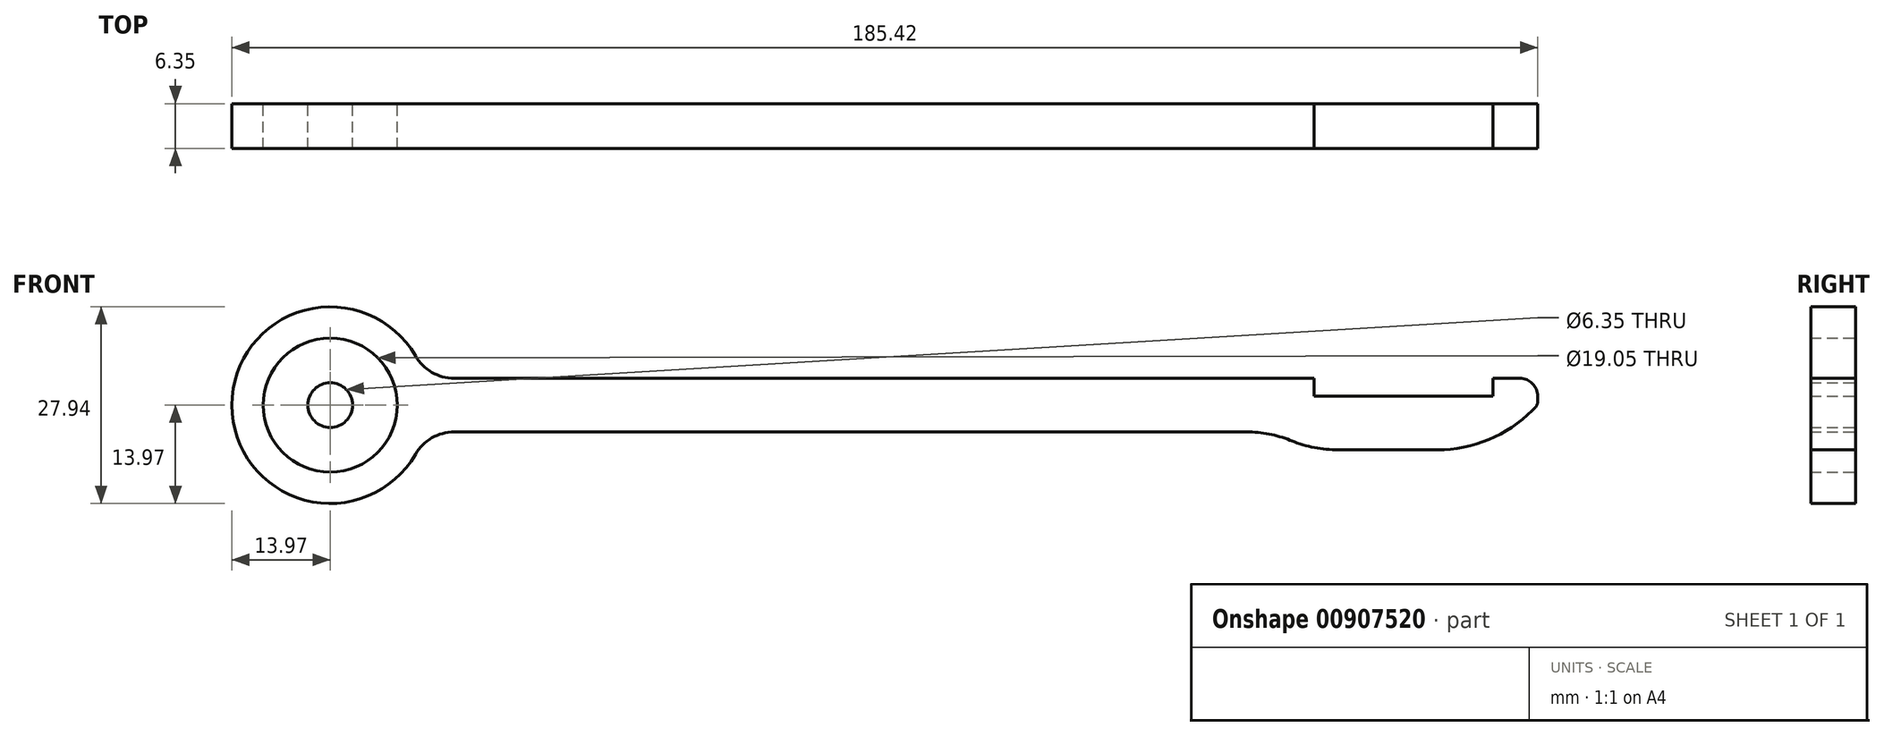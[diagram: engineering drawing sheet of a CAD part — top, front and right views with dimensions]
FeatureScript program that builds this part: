
annotation { "Feature Type Name" : "Feature", "Feature Type Description" : "" }
export const myFeature = defineFeature(function(context is Context, id is Id, definition is map)
    precondition{}
    {
        {
            var Q0;
            Q0=qCreatedBy(makeId("Front.planeOp"),FACE);
            var sketch = newSketch(context, id + "F0", { "sketchPlane" : qUnion([Q0])});
            skCircle(sketch, "E0", {"center": v(0, 0) * mm, "radius": 9.53 * mm});
            skArc(sketch, "E1", {"start": v(12.1, 6.99) * mm, "mid": v(-13.97, 0) * mm, "end": v(12.1, -6.98) * mm});
            skLineSegment(sketch, "E2", {"start": v(17.6, 3.81) * mm, "end": v(139.7, 3.81) * mm});
            skLineSegment(sketch, "E3", {"start": v(139.7, 3.81) * mm, "end": v(139.7, 1.27) * mm});
            skLineSegment(sketch, "E4", {"start": v(139.7, 1.27) * mm, "end": v(165.1, 1.27) * mm});
            skLineSegment(sketch, "E5", {"start": v(165.1, 1.27) * mm, "end": v(165.1, 3.81) * mm});
            skLineSegment(sketch, "E6", {"start": v(165.1, 3.81) * mm, "end": v(168.9, 3.81) * mm});
            skLineSegment(sketch, "E7", {"start": v(171.45, 1.27) * mm, "end": v(171.45, 0.53) * mm});
            skLineSegment(sketch, "E8", {"start": v(171.08, -0.37) * mm, "end": v(170.68, -0.77) * mm});
            skLineSegment(sketch, "E9", {"start": v(157.2, -6.35) * mm, "end": v(143.12, -6.35) * mm});
            skLineSegment(sketch, "E10", {"start": v(136.52, -5.08) * mm, "end": v(136.3, -5) * mm});
            skLineSegment(sketch, "E11", {"start": v(130.17, -3.8) * mm, "end": v(17.6, -3.8) * mm});
            skPoint(sketch, "E12", {"position": v(152.4, 1.27) * mm});
            skPoint(sketch, "E13.visualSharp", {"position": v(139.7, -6.35) * mm});
            skArc(sketch, "E13.filletArc", {"start": v(136.52, -5.08) * mm, "mid": v(139.76, -6.03) * mm, "end": v(143.12, -6.35) * mm});
            skPoint(sketch, "E14.visualSharp", {"position": v(165.1, -6.35) * mm});
            skArc(sketch, "E14.filletArc", {"start": v(157.2, -6.35) * mm, "mid": v(164.5, -4.9) * mm, "end": v(170.68, -0.77) * mm});
            skPoint(sketch, "E15.visualSharp", {"position": v(133.35, -3.8) * mm});
            skArc(sketch, "E15.filletArc", {"start": v(136.3, -5) * mm, "mid": v(133.3, -4.1) * mm, "end": v(130.17, -3.8) * mm});
            skPoint(sketch, "E16.visualSharp", {"position": v(171.45, 3.81) * mm});
            skArc(sketch, "E16.filletArc", {"start": v(171.45, 1.27) * mm, "mid": v(170.7, 3.07) * mm, "end": v(168.9, 3.81) * mm});
            skPoint(sketch, "E17.visualSharp", {"position": v(171.45, 0) * mm});
            skArc(sketch, "E17.filletArc", {"start": v(171.08, -0.37) * mm, "mid": v(171.35, 0.04) * mm, "end": v(171.45, 0.53) * mm});
            skPoint(sketch, "E18.visualSharp", {"position": v(13.44, 3.81) * mm});
            skArc(sketch, "E18.filletArc", {"start": v(12.1, 6.99) * mm, "mid": v(14.42, 4.66) * mm, "end": v(17.6, 3.81) * mm});
            skPoint(sketch, "E19.visualSharp", {"position": v(13.44, -3.8) * mm});
            skArc(sketch, "E19.filletArc", {"start": v(17.6, -3.8) * mm, "mid": v(14.42, -4.66) * mm, "end": v(12.1, -6.98) * mm});
            skSolve(sketch);
        }
        {
            var Q0;
            Q0 = qSketchRegion(id + "F0", true);
            extrude(context, id + "F1", {"entities" : qUnion([Q0]), "depth" : 6.35 * mm, "offsetDistance" : 25.4 * mm});
        }
        {
            var Q0;
            Q0=qCreatedBy(makeId("Front.planeOp"),FACE);
            var sketch = newSketch(context, id + "F2", { "sketchPlane" : qUnion([Q0])});
            skCircle(sketch, "E20", {"center": v(0, 0) * mm, "radius": 3.18 * mm});
            skCircle(sketch, "E21", {"center": v(0, 0) * mm, "radius": 9.53 * mm});
            skSolve(sketch);
        }
        {
            var Q0;
            Q0 = qSketchRegion(id + "F2", true);
            extrude(context, id + "F3", {"entities" : qUnion([Q0]), "depth" : 6.35 * mm, "offsetDistance" : 25.4 * mm});
        }
    });
